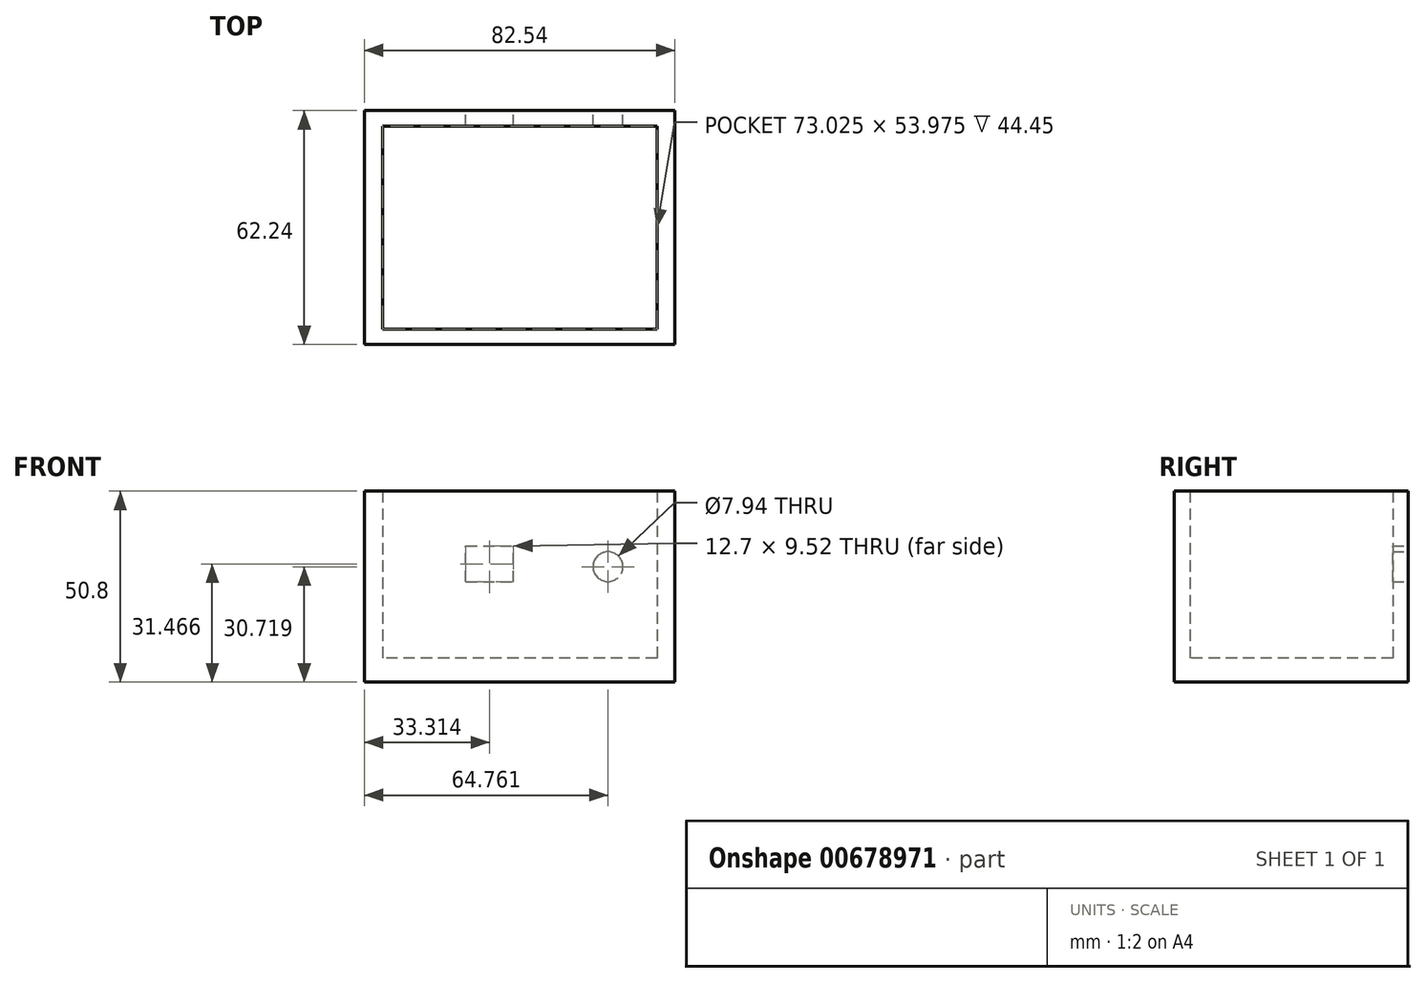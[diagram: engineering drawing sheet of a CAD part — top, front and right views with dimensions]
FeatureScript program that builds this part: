
annotation { "Feature Type Name" : "Feature", "Feature Type Description" : "" }
export const myFeature = defineFeature(function(context is Context, id is Id, definition is map)
    precondition{}
    {
        {
            var Q0;
            Q0=qCreatedBy(makeId("Top.planeOp"),FACE);
            var sketch = newSketch(context, id + "F0", { "sketchPlane" : qUnion([Q0])});
            skLineSegment(sketch, "E0.bottom", {"start": v(41.27, 31.12) * mm, "end": v(-41.28, 31.12) * mm});
            skLineSegment(sketch, "E0.top", {"start": v(41.28, -31.11) * mm, "end": v(-41.27, -31.12) * mm});
            skLineSegment(sketch, "E0.left", {"start": v(41.27, 31.12) * mm, "end": v(41.28, -31.12) * mm});
            skLineSegment(sketch, "E0.right", {"start": v(-41.28, 31.11) * mm, "end": v(-41.27, -31.12) * mm});
            skPoint(sketch, "E0.middle", {"position": v(0, 0) * mm});
            skLineSegment(sketch, "E1.bottom", {"start": v(36.51, 26.99) * mm, "end": v(-36.51, 26.99) * mm});
            skLineSegment(sketch, "E1.top", {"start": v(36.51, -26.99) * mm, "end": v(-36.51, -26.99) * mm});
            skLineSegment(sketch, "E1.left", {"start": v(36.51, 26.99) * mm, "end": v(36.51, -26.99) * mm});
            skLineSegment(sketch, "E1.right", {"start": v(-36.51, 26.99) * mm, "end": v(-36.51, -26.99) * mm});
            skSolve(sketch);
        }
        {
            var Q0;
            Q0 = qSketchRegion(id + "F0", true);
            extrude(context, id + "F1", {"entities" : qUnion([Q0]), "depth" : 50.8 * mm, "offsetDistance" : 25.4 * mm});
        }
        {
            var Q0;
            Q0=makeQuery(id+"F0.imprint","IMPRINT",FACE,{"disambiguationData":[TD([[makeQuery(id+"F0.imprint","IMPRINT",EDGE,{"derivedFrom":sQuery(id+"F0.wireOp",EDGE,"E1.bottom")}),1.0]])]});
            extrude(context, id + "F2", {"entities" : qUnion([Q0]), "operationType" : NewBodyOperationType.ADD, "depth" : 6.35 * mm, "offsetDistance" : 25.4 * mm});
        }
        {
            var Q0;
            Q0=makeQuery(id+"F1.opExtrude","SWEPT_FACE",FACE,{"disambiguationData":[OSD([sQuery(id+"F0.wireOp",EDGE,"E0.bottom")])]});
            var sketch = newSketch(context, id + "F3", { "sketchPlane" : qUnion([Q0])});
            skCircle(sketch, "E2", {"center": v(-23.5, 30.72) * mm, "radius": 3.97 * mm});
            skLineSegment(sketch, "E3.bottom", {"start": v(14.3, 26.7) * mm, "end": v(1.6, 26.7) * mm});
            skLineSegment(sketch, "E3.top", {"start": v(14.3, 36.23) * mm, "end": v(1.6, 36.23) * mm});
            skLineSegment(sketch, "E3.left", {"start": v(14.3, 26.7) * mm, "end": v(14.3, 36.23) * mm});
            skLineSegment(sketch, "E3.right", {"start": v(1.6, 26.7) * mm, "end": v(1.6, 36.23) * mm});
            skPoint(sketch, "E3.middle", {"position": v(7.96, 31.47) * mm});
            skSolve(sketch);
        }
        {
            var Q0;
            Q0=makeQuery(id+"F3.imprint","IMPRINT",FACE,{"disambiguationData":[TD([[makeQuery(id+"F3.imprint","IMPRINT",EDGE,{"derivedFrom":sQuery(id+"F3.wireOp",EDGE,"E2")}),1.0]])]});
            extrude(context, id + "F4", {"entities" : qUnion([Q0]), "operationType" : NewBodyOperationType.REMOVE, "endBound" : BoundingType.UP_TO_NEXT, "oppositeDirection" : true, "depth" : 8.38 * mm, "offsetDistance" : 25.4 * mm});
        }
        {
            var Q0;
            Q0=makeQuery(id+"F3.imprint","IMPRINT",FACE,{"disambiguationData":[TD([[makeQuery(id+"F3.imprint","IMPRINT",EDGE,{"derivedFrom":sQuery(id+"F3.wireOp",EDGE,"E3.bottom")}),-1.0]])]});
            extrude(context, id + "F5", {"entities" : qUnion([Q0]), "operationType" : NewBodyOperationType.REMOVE, "endBound" : BoundingType.UP_TO_NEXT, "oppositeDirection" : true, "depth" : 25.4 * mm, "offsetDistance" : 25.4 * mm});
        }
    });
